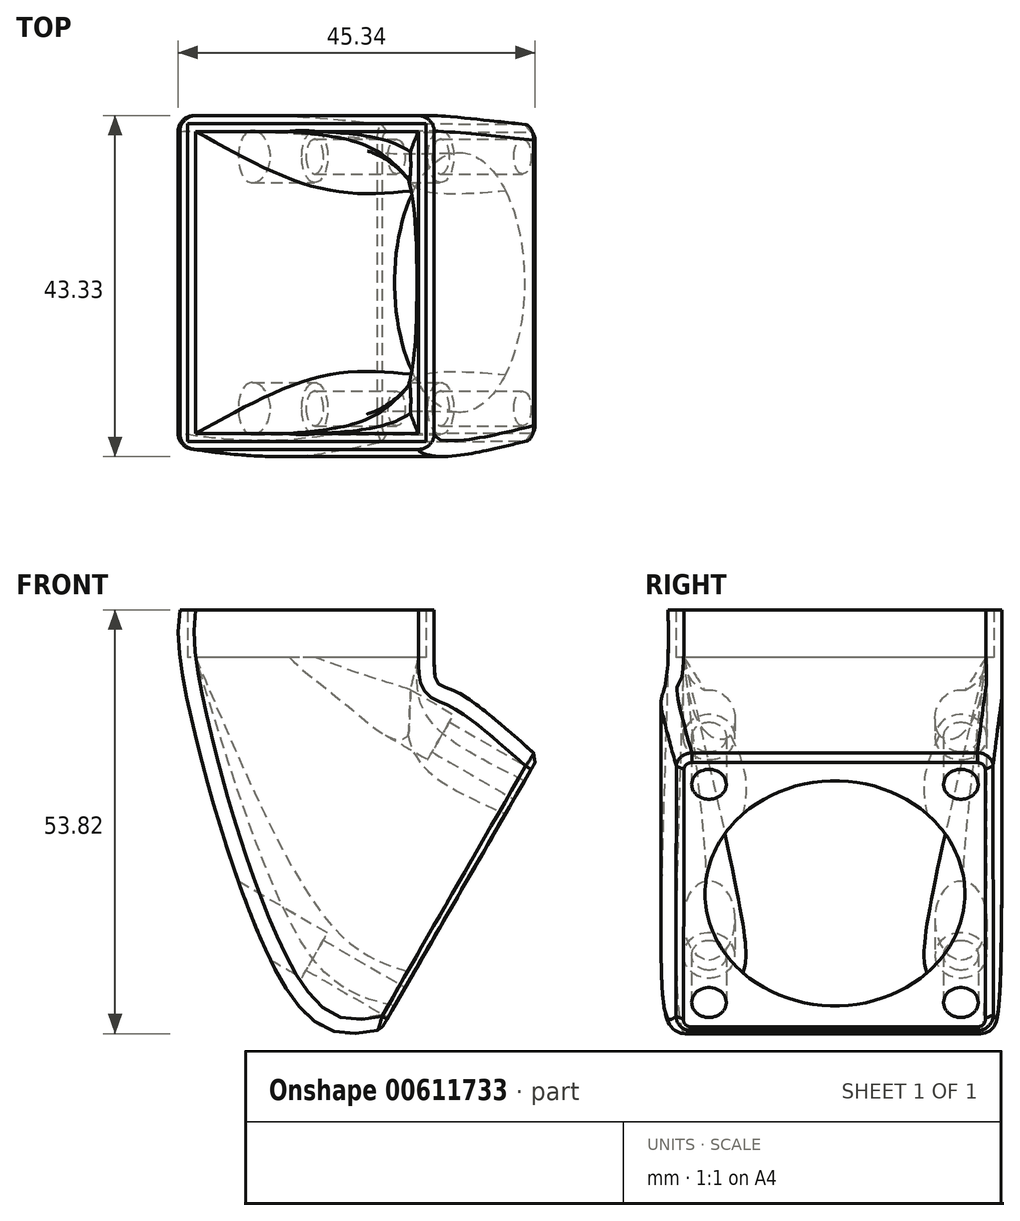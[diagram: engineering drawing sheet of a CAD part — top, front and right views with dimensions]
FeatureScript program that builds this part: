
annotation { "Feature Type Name" : "Feature", "Feature Type Description" : "" }
export const myFeature = defineFeature(function(context is Context, id is Id, definition is map)
    precondition{}
    {
        {
            var Q0;
            Q0=qCreatedBy(makeId("Top.planeOp"),FACE);
            var sketch = newSketch(context, id + "F0", { "sketchPlane" : qUnion([Q0])});
            skLineSegment(sketch, "E0", {"start": v(0, -58.01) * mm, "end": v(0, 90.59) * mm, "construction": true});
            skSolve(sketch);
        }
        {
            var Q0;
            Q0=sQuery(id+"F0.wireOp",EDGE,"E0");
            var Q1;
            Q1=qCreatedBy(makeId("Top.planeOp"),FACE);
            cPlane(context, id + "F1", {"entities" : qUnion([Q0, Q1]), "cplaneType" : CPlaneType.LINE_ANGLE, "offset" : 25 * mm, "angle" : 60 * degree, "oppositeDirection" : true, "width" : 150 * mm, "height" : 150 * mm});
        }
        {
            var Q0;
            Q0=qCreatedBy(id+"F1.planeOp",FACE);
            var sketch = newSketch(context, id + "F2", { "sketchPlane" : qUnion([Q0])});
            skLineSegment(sketch, "E1.bottom", {"start": v(16, 16) * mm, "end": v(-16, 16) * mm, "construction": true});
            skLineSegment(sketch, "E1.top", {"start": v(16, -16) * mm, "end": v(-16, -16) * mm, "construction": true});
            skLineSegment(sketch, "E1.left", {"start": v(16, 16) * mm, "end": v(16, -16) * mm, "construction": true});
            skLineSegment(sketch, "E1.right", {"start": v(-16, 16) * mm, "end": v(-16, -16) * mm, "construction": true});
            skPoint(sketch, "E1.middle", {"position": v(0, 0) * mm});
            skLineSegment(sketch, "E2.bottom", {"start": v(20, 20) * mm, "end": v(-20, 20) * mm});
            skLineSegment(sketch, "E2.top", {"start": v(20, -20) * mm, "end": v(-20, -20) * mm});
            skLineSegment(sketch, "E2.left", {"start": v(20, 20) * mm, "end": v(20, -20) * mm});
            skLineSegment(sketch, "E2.right", {"start": v(-20, 20) * mm, "end": v(-20, -20) * mm});
            skCircle(sketch, "E3", {"center": v(0, 0) * mm, "radius": 16.5 * mm, "construction": true});
            skSolve(sketch);
        }
        {
            var Q0;
            Q0=makeQuery(id+"F2.imprint","IMPRINT",FACE,{"disambiguationData":[TD([[makeQuery(id+"F2.imprint","IMPRINT",EDGE,{"derivedFrom":sQuery(id+"F2.wireOp",EDGE,"E2.bottom")}),1.0]])]});
            var sketch = newSketch(context, id + "F3", { "sketchPlane" : qUnion([Q0])});
            skCircle(sketch, "E4.0", {"center": v(0, 0) * mm, "radius": 16.5 * mm});
            skCircle(sketch, "E5.cCircle", {"center": v(0, 0) * mm, "radius": 16.5 * mm, "construction": true});
            skLineSegment(sketch, "E5.0", {"start": v(11.67, 11.67) * mm, "end": v(11.67, -11.67) * mm, "construction": true});
            skLineSegment(sketch, "E5.1", {"start": v(11.67, -11.67) * mm, "end": v(-11.67, -11.67) * mm, "construction": true});
            skLineSegment(sketch, "E5.2", {"start": v(-11.67, -11.67) * mm, "end": v(-11.67, 11.67) * mm, "construction": true});
            skLineSegment(sketch, "E5.3", {"start": v(-11.67, 11.67) * mm, "end": v(11.67, 11.67) * mm, "construction": true});
            skSolve(sketch);
        }
        {
            var Q0;
            Q0=qCreatedBy(makeId("Top.planeOp"),FACE);
            cPlane(context, id + "F4", {"entities" : qUnion([Q0]), "cplaneType" : CPlaneType.OFFSET, "offset" : 30 * mm, "width" : 150 * mm, "height" : 150 * mm});
        }
        {
            var Q0;
            Q0=qCreatedBy(id+"F4.planeOp",FACE);
            var sketch = newSketch(context, id + "F5", { "sketchPlane" : qUnion([Q0])});
            skLineSegment(sketch, "E6.bottom", {"start": v(-3.23, 21.2) * mm, "end": v(-35.53, 21.2) * mm});
            skLineSegment(sketch, "E6.top", {"start": v(-3.23, -21.2) * mm, "end": v(-35.53, -21.2) * mm});
            skLineSegment(sketch, "E6.left", {"start": v(-3.23, 21.2) * mm, "end": v(-3.23, -21.2) * mm});
            skLineSegment(sketch, "E6.right", {"start": v(-35.53, 21.2) * mm, "end": v(-35.53, -21.2) * mm});
            skPoint(sketch, "E6.middle", {"position": v(-19.38, 0) * mm});
            skSolve(sketch);
        }
        {
            var Q0;
            Q0=makeQuery(id+"F5.imprint","IMPRINT",FACE,{"disambiguationData":[TD([[makeQuery(id+"F5.imprint","IMPRINT",EDGE,{"derivedFrom":sQuery(id+"F5.wireOp",EDGE,"E6.bottom")}),1.0]])]});
            var sketch = newSketch(context, id + "F6", { "sketchPlane" : qUnion([Q0])});
            skPoint(sketch, "E7.0", {"position": v(-19.38, 0) * mm});
            skLineSegment(sketch, "E8.bottom", {"start": v(-4.23, 20.2) * mm, "end": v(-34.53, 20.2) * mm});
            skLineSegment(sketch, "E8.top", {"start": v(-4.23, -20.2) * mm, "end": v(-34.53, -20.2) * mm});
            skLineSegment(sketch, "E8.left", {"start": v(-4.23, 20.2) * mm, "end": v(-4.23, -20.2) * mm});
            skLineSegment(sketch, "E8.right", {"start": v(-34.53, 20.2) * mm, "end": v(-34.53, -20.2) * mm});
            skLineSegment(sketch, "E9.0", {"start": v(-33.53, 19.2) * mm, "end": v(-33.53, -19.2) * mm});
            skLineSegment(sketch, "E9.1", {"start": v(-5.23, 19.2) * mm, "end": v(-33.53, 19.2) * mm});
            skLineSegment(sketch, "E9.2", {"start": v(-5.23, 19.2) * mm, "end": v(-5.23, -19.2) * mm});
            skLineSegment(sketch, "E9.3", {"start": v(-5.23, -19.2) * mm, "end": v(-33.53, -19.2) * mm});
            skSolve(sketch);
        }
        {
            var Q0;
            Q0=qCreatedBy(id+"F1.planeOp",FACE);
            cPlane(context, id + "F7", {"entities" : qUnion([Q0]), "cplaneType" : CPlaneType.OFFSET, "offset" : 12 * mm, "oppositeDirection" : true, "width" : 150 * mm, "height" : 150 * mm});
        }
        {
            var Q0;
            Q0=qCreatedBy(id+"F7.planeOp",FACE);
            var sketch = newSketch(context, id + "F8", { "sketchPlane" : qUnion([Q0])});
            skLineSegment(sketch, "E10.0.0", {"start": v(-22, -22) * mm, "end": v(21, -22) * mm});
            skLineSegment(sketch, "E10.0.1", {"start": v(21, -22) * mm, "end": v(21, 22) * mm});
            skLineSegment(sketch, "E10.0.2", {"start": v(21, 22) * mm, "end": v(-22, 22) * mm});
            skLineSegment(sketch, "E10.0.3", {"start": v(-22, 22) * mm, "end": v(-22, -22) * mm});
            skCircle(sketch, "E11.0", {"center": v(0, 0) * mm, "radius": 16.5 * mm, "construction": true});
            skLineSegment(sketch, "E12.0", {"start": v(-16, 16) * mm, "end": v(-16, -16) * mm, "construction": true});
            skLineSegment(sketch, "E12.1", {"start": v(16, 16) * mm, "end": v(-16, 16) * mm, "construction": true});
            skLineSegment(sketch, "E12.2", {"start": v(16, 16) * mm, "end": v(16, -16) * mm, "construction": true});
            skLineSegment(sketch, "E12.3", {"start": v(16, -16) * mm, "end": v(-16, -16) * mm, "construction": true});
            skSolve(sketch);
        }
        {
            var Q0;
            Q0=makeQuery(id+"F8.imprint","IMPRINT",FACE,{"disambiguationData":[TD([[makeQuery(id+"F8.imprint","IMPRINT",EDGE,{"derivedFrom":sQuery(id+"F8.wireOp",EDGE,"E10.0.0")}),1.0]])]});
            var sketch = newSketch(context, id + "F9", { "sketchPlane" : qUnion([Q0])});
            skCircle(sketch, "E13.0", {"center": v(0, 0) * mm, "radius": 16.5 * mm});
            skCircle(sketch, "E14.cCircle", {"center": v(0, 0) * mm, "radius": 16.5 * mm, "construction": true});
            skLineSegment(sketch, "E14.0", {"start": v(-11.67, -11.67) * mm, "end": v(-11.67, 11.67) * mm, "construction": true});
            skLineSegment(sketch, "E14.1", {"start": v(-11.67, 11.67) * mm, "end": v(11.67, 11.67) * mm, "construction": true});
            skLineSegment(sketch, "E14.2", {"start": v(11.67, 11.67) * mm, "end": v(11.67, -11.67) * mm, "construction": true});
            skLineSegment(sketch, "E14.3", {"start": v(11.67, -11.67) * mm, "end": v(-11.67, -11.67) * mm, "construction": true});
            skSolve(sketch);
        }
        {
            var Q0;
            Q0=qCreatedBy(id+"F4.planeOp",FACE);
            cPlane(context, id + "F10", {"entities" : qUnion([Q0]), "cplaneType" : CPlaneType.OFFSET, "offset" : 6 * mm, "width" : 150 * mm, "height" : 150 * mm});
        }
        {
            var Q0;
            Q0=qCreatedBy(id+"F10.planeOp",FACE);
            var sketch = newSketch(context, id + "F11", { "sketchPlane" : qUnion([Q0])});
            skLineSegment(sketch, "E15.0", {"start": v(-35.53, 21.2) * mm, "end": v(-35.53, -21.2) * mm});
            skLineSegment(sketch, "E15.1", {"start": v(-3.23, -21.2) * mm, "end": v(-35.53, -21.2) * mm});
            skLineSegment(sketch, "E15.2", {"start": v(-3.23, 21.2) * mm, "end": v(-3.23, -21.2) * mm});
            skLineSegment(sketch, "E15.3", {"start": v(-3.23, 21.2) * mm, "end": v(-35.53, 21.2) * mm});
            skSolve(sketch);
        }
        {
            var Q0;
            Q0=makeQuery(id+"F11.imprint","IMPRINT",FACE,{"disambiguationData":[TD([[makeQuery(id+"F11.imprint","IMPRINT",EDGE,{"derivedFrom":sQuery(id+"F11.wireOp",EDGE,"E15.0")}),1.0]])]});
            var Q1;
            Q1=makeQuery(id+"F5.imprint","IMPRINT",FACE,{"disambiguationData":[TD([[makeQuery(id+"F5.imprint","IMPRINT",EDGE,{"derivedFrom":sQuery(id+"F5.wireOp",EDGE,"E6.bottom")}),1.0]])]});
            var Q2;
            Q2=makeQuery(id+"F8.imprint","IMPRINT",FACE,{"disambiguationData":[TD([[makeQuery(id+"F8.imprint","IMPRINT",EDGE,{"derivedFrom":sQuery(id+"F8.wireOp",EDGE,"E10.0.0")}),1.0]])]});
            var Q3;
            Q3=makeQuery(id+"F2.imprint","IMPRINT",FACE,{"disambiguationData":[TD([[makeQuery(id+"F2.imprint","IMPRINT",EDGE,{"derivedFrom":sQuery(id+"F2.wireOp",EDGE,"E2.bottom")}),1.0]])]});
            loft(context, id + "F12", {"sheetProfilesArray" : [{ "sheetProfileEntities" : qUnion([Q0]) }, { "sheetProfileEntities" : qUnion([Q1]) }, { "sheetProfileEntities" : qUnion([Q2]) }, { "sheetProfileEntities" : qUnion([Q3]) }]});
        }
        {
            var Q1;
            Q1=makeQuery(id+"F6.imprint","IMPRINT",FACE,{"disambiguationData":[TD([[makeQuery(id+"F6.imprint","IMPRINT",EDGE,{"derivedFrom":sQuery(id+"F6.wireOp",EDGE,"E9.0")}),1.0]])]});
            var Q2;
            Q2=makeQuery(id+"F9.imprint","IMPRINT",FACE,{"disambiguationData":[TD([[makeQuery(id+"F9.imprint","IMPRINT",EDGE,{"derivedFrom":sQuery(id+"F9.wireOp",EDGE,"E13.0")}),1.0]])]});
            var Q3;
            Q3=makeQuery(id+"F3.imprint","IMPRINT",FACE,{"disambiguationData":[TD([[makeQuery(id+"F3.imprint","IMPRINT",EDGE,{"derivedFrom":sQuery(id+"F3.wireOp",EDGE,"E4.0")}),1.0]])]});
            var Q4;
            Q4=sQuery(id+"F6.wireOp",VERTEX,"E9.1.end");
            var Q5;
            Q5=sQuery(id+"F9.wireOp",VERTEX,"E14.3.start");
            var Q6;
            Q6=sQuery(id+"F3.wireOp",VERTEX,"E5.1.start");
            loft(context, id + "F13", {"operationType" : NewBodyOperationType.REMOVE, "sheetProfilesArray" : [{ "sheetProfileEntities" : qUnion([Q1]) }, { "sheetProfileEntities" : qUnion([Q2]) }, { "sheetProfileEntities" : qUnion([Q3]) }], "matchConnections" : true, "connections" : [{ "connectionEntities" : qUnion([Q4, Q5, Q6]), "connectionEdgeQueries" : qUnion([]), "connectionEdgeParameters" : [] }]});
        }
        {
            var Q0;
            Q0=makeQuery(id+"F6.imprint","IMPRINT",FACE,{"disambiguationData":[TD([[makeQuery(id+"F6.imprint","IMPRINT",EDGE,{"derivedFrom":sQuery(id+"F6.wireOp",EDGE,"E8.bottom")}),1.0]])]});
            var Q1;
            Q1=makeQuery(id+"F6.imprint","IMPRINT",FACE,{"disambiguationData":[TD([[makeQuery(id+"F6.imprint","IMPRINT",EDGE,{"derivedFrom":sQuery(id+"F6.wireOp",EDGE,"E9.0")}),1.0]])]});
            extrude(context, id + "F14", {"entities" : qUnion([Q0, Q1]), "operationType" : NewBodyOperationType.REMOVE, "endBound" : BoundingType.UP_TO_NEXT, "depth" : 25 * mm, "offsetDistance" : 25 * mm});
        }
        {
            var Q0;
            Q0=makeQuery(id+"F12.opLoft","SWEPT_EDGE",EDGE,{"disambiguationData":[OSD([sQuery(id+"F5.wireOp",EDGE,"E6.top"),sQuery(id+"F5.wireOp",EDGE,"E6.right"),sQuery(id+"F11.wireOp",EDGE,"E15.0"),sQuery(id+"F11.wireOp",EDGE,"E15.1")])]});
            var Q1;
            Q1=makeQuery(id+"F12.opLoft","SWEPT_EDGE",EDGE,{"disambiguationData":[OSD([sQuery(id+"F5.wireOp",EDGE,"E6.top"),sQuery(id+"F5.wireOp",EDGE,"E6.left"),sQuery(id+"F11.wireOp",EDGE,"E15.1"),sQuery(id+"F11.wireOp",EDGE,"E15.2")])]});
            var Q2;
            Q2=makeQuery(id+"F12.opLoft","SWEPT_EDGE",EDGE,{"disambiguationData":[OSD([sQuery(id+"F5.wireOp",EDGE,"E6.bottom"),sQuery(id+"F5.wireOp",EDGE,"E6.left"),sQuery(id+"F11.wireOp",EDGE,"E15.2"),sQuery(id+"F11.wireOp",EDGE,"E15.3")])]});
            var Q3;
            Q3=makeQuery(id+"F12.opLoft","SWEPT_EDGE",EDGE,{"disambiguationData":[OSD([sQuery(id+"F5.wireOp",EDGE,"E6.bottom"),sQuery(id+"F5.wireOp",EDGE,"E6.right"),sQuery(id+"F11.wireOp",EDGE,"E15.0"),sQuery(id+"F11.wireOp",EDGE,"E15.3")])]});
            fillet(context, id + "F15", {"entities" : qUnion([Q0, Q1, Q2, Q3]), "radius" : 2 * mm, "tangentPropagation" : true, "allowEdgeOverflow" : false});
        }
        {
            var Q0;
            Q0=sQuery(id+"F2.wireOp",VERTEX,"E1.left.start");
            var Q1;
            Q1=sQuery(id+"F2.wireOp",VERTEX,"E1.left.end");
            var Q2;
            Q2=sQuery(id+"F2.wireOp",VERTEX,"E1.right.end");
            var Q3;
            Q3=sQuery(id+"F2.wireOp",VERTEX,"E1.right.start");
            var Q4;
            Q4=makeQuery(id+"F12.opLoft","SWEPT_BODY",BODY,{"disambiguationData":[OSD([makeQuery(id+"F2.imprint","IMPRINT",FACE,{"disambiguationData":[TD([[makeQuery(id+"F2.imprint","IMPRINT",EDGE,{"derivedFrom":sQuery(id+"F2.wireOp",EDGE,"E2.bottom")}),1.0]])]}),sQuery(id+"F5.wireOp",EDGE,"E6.bottom"),sQuery(id+"F8.wireOp",EDGE,"E10.0.0"),makeQuery(id+"F11.imprint","IMPRINT",FACE,{"disambiguationData":[TD([[makeQuery(id+"F11.imprint","IMPRINT",EDGE,{"derivedFrom":sQuery(id+"F11.wireOp",EDGE,"E15.0")}),1.0]])]})])]});
            hole(context, id + "F16", {"style" : HoleStyle.SIMPLE, "endStyle" : HoleEndStyle.BLIND, "standardTappedOrClearance" : lookupTablePath({ "standard" : "ISO", "fit" : "Normal", "size" : "M4", "type" : "Clearance" }), "standardBlindInLast" : lookupTablePath({ "fit" : "Standard", "standard" : "ISO", "size" : "M4", "type" : "Clearance" }), "holeDiameter" : 4.4 * mm, "majorDiameter" : 5 * mm, "holeDepth" : 12 * mm, "isTappedThrough" : true, "tappedDepth" : 12 * mm, "tapClearance" : 3, "startFromSketch" : true, "locations" : qUnion([Q0, Q1, Q2, Q3]), "scope" : qUnion([Q4])});
        }
        {
            var Q0;
            Q0=sQuery(id+"F8.wireOp",VERTEX,"E12.3.start");
            var Q1;
            Q1=sQuery(id+"F8.wireOp",VERTEX,"E12.3.end");
            var Q2;
            Q2=sQuery(id+"F8.wireOp",VERTEX,"E12.1.end");
            var Q3;
            Q3=sQuery(id+"F8.wireOp",VERTEX,"E12.2.start");
            var Q4;
            Q4=makeQuery(id+"F12.opLoft","SWEPT_BODY",BODY,{"disambiguationData":[OSD([makeQuery(id+"F2.imprint","IMPRINT",FACE,{"disambiguationData":[TD([[makeQuery(id+"F2.imprint","IMPRINT",EDGE,{"derivedFrom":sQuery(id+"F2.wireOp",EDGE,"E2.bottom")}),1.0]])]}),sQuery(id+"F5.wireOp",EDGE,"E6.bottom"),sQuery(id+"F8.wireOp",EDGE,"E10.0.0"),makeQuery(id+"F11.imprint","IMPRINT",FACE,{"disambiguationData":[TD([[makeQuery(id+"F11.imprint","IMPRINT",EDGE,{"derivedFrom":sQuery(id+"F11.wireOp",EDGE,"E15.0")}),1.0]])]})])]});
            hole(context, id + "F17", {"style" : HoleStyle.SIMPLE, "endStyle" : HoleEndStyle.BLIND, "standardTappedOrClearance" : lookupTablePath({ "standard" : "ISO", "fit" : "Normal", "size" : "M6", "type" : "Clearance" }), "standardBlindInLast" : lookupTablePath({ "fit" : "Standard", "standard" : "ISO", "size" : "M6", "type" : "Clearance" }), "holeDiameter" : 6.6 * mm, "majorDiameter" : 6 * mm, "holeDepth" : 22 * mm, "isTappedThrough" : true, "tappedDepth" : 12 * mm, "tapClearance" : 3, "startFromSketch" : true, "locations" : qUnion([Q0, Q1, Q2, Q3]), "scope" : qUnion([Q4])});
        }
        {
            var Q0;
            Q0=makeQuery(id+"F15.opFillet","BLEND_EDGE",EDGE,{"blendedFrom":[makeQuery(id+"F12.opLoft","SWEPT_EDGE",EDGE,{"disambiguationData":[OSD([sQuery(id+"F5.wireOp",EDGE,"E6.top"),sQuery(id+"F5.wireOp",EDGE,"E6.left"),sQuery(id+"F11.wireOp",EDGE,"E15.1"),sQuery(id+"F11.wireOp",EDGE,"E15.2")])]}),makeQuery(id+"F12.opLoft","CAP_FACE",FACE,{"disambiguationData":[OSD([makeQuery(id+"F2.imprint","IMPRINT",FACE,{"disambiguationData":[TD([[makeQuery(id+"F2.imprint","IMPRINT",EDGE,{"derivedFrom":sQuery(id+"F2.wireOp",EDGE,"E2.bottom")}),1.0]])]})])],"isStart":true})],"blendedInto":[makeQuery(id+"F12.opLoft","CAP_FACE",FACE,{"disambiguationData":[OSD([makeQuery(id+"F2.imprint","IMPRINT",FACE,{"disambiguationData":[TD([[makeQuery(id+"F2.imprint","IMPRINT",EDGE,{"derivedFrom":sQuery(id+"F2.wireOp",EDGE,"E2.bottom")}),1.0]])]})])],"isStart":true})]});
            chamfer(context, id + "F18", {"entities" : qUnion([Q0]), "width" : 1 * mm, "tangentPropagation" : true});
        }
    });
